FCSTD DOCUMENT  (FreeCAD 0.20R29410 (Git))
Label: ASM_Main
License: All rights reserved
LicenseURL: http://en.wikipedia.org/wiki/All_rights_reserved
objects: App::Link×4, App::DocumentObjectGroup×3, PartDesign::CoordinateSystem×1, App::FeaturePython×1, App::Part×1
note: 1 computed .brp shape members not serialized (recipe doc carries the construction recipe); baked Part::Feature solids carry a one-line shape summary decoded from their .brp
EXTERNAL_REF file=ASM_Base.FCStd obj=LCS_Origin
EXTERNAL_REF file=ASM_Base.FCStd obj=Assembly
EXTERNAL_REF file=ASM_Base.FCStd obj=PillowBlock_LCS_0
EXTERNAL_REF file=ASM_Platform.FCStd obj=ComputerPlatform_LCS_TopPivot
EXTERNAL_REF file=ASM_Platform.FCStd obj=Assembly
EXTERNAL_REF file=PlayStation5.FCStd obj=LCS_Origin
EXTERNAL_REF file=PlayStation5.FCStd obj=Assembly
EXTERNAL_REF file=ASM_DrivePlatform.FCStd obj=LCS_Origin
EXTERNAL_REF file=ASM_Platform.FCStd obj=LCS_Origin
EXTERNAL_REF file=ASM_DrivePlatform.FCStd obj=Assembly

FEATURE [App::DocumentObjectGroup] Parts
FEATURE [PartDesign::CoordinateSystem] LCS_Origin
  AttacherType = Attacher::AttachEngine3D
  MapMode = 2
  Support = -> [X_Axis]
FEATURE [App::FeaturePython] Variables  # WARN: FeaturePython — macro-defined, semantics opaque (R4)
  Type = App::PropertyContainer
FEATURE [App::DocumentObjectGroup] Constraints
FEATURE [App::DocumentObjectGroup] Configurations
FEATURE [App::Link] ASM_Base
  AttachedBy = #LCS_Origin
  AttachedTo = Parent Assembly#LCS_Origin
  LinkedObject = -> <external ASM_Base.FCStd>#Assembly
  SolverId = Asm4EE
  expr: Placement = LCS_Origin.Placement * AttachmentOffset * ASM_Base#LCS_Origin.Placement ^ -1
FEATURE [App::Link] ASM_Platform
  AttachedBy = #ComputerPlatform_LCS_TopPivot
  AttachedTo = ASM_Base#PillowBlock_LCS_0
  LinkPlacement = pos=(0,-1.75e-14,-124.8) rot=(0,0,1;0rad)
  LinkedObject = -> <external ASM_Platform.FCStd>#Assembly
  Placement = pos=(0,-1.75e-14,-124.8) rot=(0,0,1;0rad)
  SolverId = Asm4EE
  expr: Placement = ASM_Base.Placement * ASM_Base#PillowBlock_LCS_0.Placement * AttachmentOffset * ASM_Platform#ComputerPlatform_LCS_TopPivot.Placement ^ -1
FEATURE [App::Link] PlayStation5
  AttachedBy = #LCS_Origin
  AttachedTo = ASM_Platform#ComputerPlatform_LCS_TopPivot
  AttachmentOffset = pos=(0,-250,0) rot=(0,0,1;1.5708rad)
  LinkPlacement = pos=(0,-250,-106.3) rot=(0,0,-1;4.71239rad)
  LinkedObject = -> <external PlayStation5.FCStd>#Assembly
  Placement = pos=(0,-250,-106.3) rot=(0,0,-1;4.71239rad)
  SolverId = Asm4EE
  expr: Placement = ASM_Platform.Placement * ASM_Platform#ComputerPlatform_LCS_TopPivot.Placement * AttachmentOffset * PlayStation5#LCS_Origin.Placement ^ -1
FEATURE [App::Link] ASM_DrivePlatform
  AttachedBy = #LCS_Origin
  AttachedTo = ASM_Platform#LCS_Origin
  AttachmentOffset = pos=(0,0,69) rot=(0,0,1;0rad)
  LinkPlacement = pos=(0,-6e-16,-55.8) rot=(0,0,1;0rad)
  LinkedObject = -> <external ASM_DrivePlatform.FCStd>#Assembly
  Placement = pos=(0,-6e-16,-55.8) rot=(0,0,1;0rad)
  SolverId = Asm4EE
  expr: Placement = ASM_Platform.Placement * ASM_Platform#LCS_Origin.Placement * AttachmentOffset * ASM_DrivePlatform#LCS_Origin.Placement ^ -1
FEATURE [App::Part] Assembly
  AssemblyType = Part::Link
  Group = -> [LCS_Origin,Variables,Constraints,Configurations,ASM_Base,ASM_Platform,PlayStation5,ASM_DrivePlatform]
  Origin = -> Origin
  Type = Assembly

RESOLVED EXTERNAL PARTS (link-assembly join: the EXTERNAL_REF files above that resolve inside this repo's crawl, each included once):
---- part ASM_Base.FCStd = doc fcstd_288255adafcc ----
FCSTD DOCUMENT  (FreeCAD 0.20R29410 (Git))
Label: ASM_Base
License: All rights reserved
LicenseURL: http://en.wikipedia.org/wiki/All_rights_reserved
objects: App::Link×5, App::DocumentObjectGroup×3, PartDesign::CoordinateSystem×2, App::FeaturePython×1, App::Part×1
note: 2 computed .brp shape members not serialized (recipe doc carries the construction recipe); baked Part::Feature solids carry a one-line shape summary decoded from their .brp
EXTERNAL_REF file=MainWheel.FCStd obj=LCS_1
EXTERNAL_REF file=MainWheel.FCStd obj=Body
EXTERNAL_REF file=PipeFloorFlange.FCStd obj=LCS_1
EXTERNAL_REF file=PipeFloorFlange.FCStd obj=Body
EXTERNAL_REF file=PipeNipple.FCStd obj=LCS_root
EXTERNAL_REF file=PipeNipple.FCStd obj=Body
EXTERNAL_REF file=PillowBlock.FCStd obj=LCS_0
EXTERNAL_REF file=PipeNipple.FCStd obj=LCS_end
EXTERNAL_REF file=PillowBlock.FCStd obj=Body
EXTERNAL_REF file=SlipRing.FCStd obj=LCS_Origin
EXTERNAL_REF file=SlipRing.FCStd obj=Assembly

FEATURE [App::DocumentObjectGroup] Parts
FEATURE [PartDesign::CoordinateSystem] LCS_Origin
  AttacherType = Attacher::AttachEngine3D
  MapMode = 2
  Support = -> [X_Axis]
FEATURE [App::FeaturePython] Variables  # WARN: FeaturePython — macro-defined, semantics opaque (R4)
  Type = App::PropertyContainer
FEATURE [App::DocumentObjectGroup] Constraints
FEATURE [App::DocumentObjectGroup] Configurations
FEATURE [App::Link] MainWheel
  AssemblyType = Part::Link
  AttachedBy = #LCS_1
  AttachedTo = Parent Assembly#LCS_Origin
  LinkedObject = -> <external MainWheel.FCStd>#Body
  SolverId = Asm4EE
  expr: Placement = LCS_Origin.Placement * AttachmentOffset * MainWheel#LCS_1.Placement ^ -1
FEATURE [App::Link] PipeFlange
  AssemblyType = Part::Link
  AttachedBy = #LCS_1
  AttachedTo = MainWheel#LCS_1
  AttachmentOffset = pos=(0,0,0) rot=(1,0,0;3.14159rad)
  LinkPlacement = pos=(0,0,0) rot=(1,0,0;3.14159rad)
  LinkedObject = -> <external PipeFloorFlange.FCStd>#Body
  Placement = pos=(0,0,0) rot=(1,0,0;3.14159rad)
  SolverId = Asm4EE
  expr: Placement = MainWheel.Placement * MainWheel#LCS_1.Placement * AttachmentOffset * PipeFloorFlange#LCS_1.Placement ^ -1
FEATURE [App::Link] PipeNipple
  AssemblyType = Part::Link
  AttachedBy = #LCS_root
  AttachedTo = PipeFlange#LCS_1
  LinkPlacement = pos=(0,0,0) rot=(1,0,0;3.14159rad)
  LinkedObject = -> <external PipeNipple.FCStd>#Body
  Placement = pos=(0,0,0) rot=(1,0,0;3.14159rad)
  SolverId = Asm4EE
  expr: Placement = PipeFlange.Placement * PipeFloorFlange#LCS_1.Placement * AttachmentOffset * PipeNipple#LCS_root.Placement ^ -1
FEATURE [App::Link] PillowBlock
  AssemblyType = Part::Link
  AttachedBy = #LCS_0
  AttachedTo = PipeNipple#LCS_end
  AttachmentOffset = pos=(0,0,-8) rot=(1,0,0;3.14159rad)
  LinkPlacement = pos=(0,-1.3e-14,-106.3) rot=(0,0,1;0rad)
  LinkedObject = -> <external PillowBlock.FCStd>#Body
  Placement = pos=(0,-1.3e-14,-106.3) rot=(0,0,1;0rad)
  SolverId = Asm4EE
  expr: Placement = PipeNipple.Placement * PipeNipple#LCS_end.Placement * AttachmentOffset * PillowBlock#LCS_0.Placement ^ -1
FEATURE [PartDesign::CoordinateSystem] PillowBlock_LCS_0
  AttachedBy = Origin
  AttacherType = Attacher::AttachEngine3D
  Placement = pos=(0,-1.3e-14,-106.3) rot=(0,0,1;0rad)
  SolverId = Asm4EE
  expr: Placement = PillowBlock.Placement * PillowBlock#LCS_0.Placement
FEATURE [App::Link] SlipRing
  AttachedBy = #LCS_Origin
  AttachedTo = PipeNipple#LCS_end
  AttachmentOffset = pos=(0,0,0) rot=(1,0,0;3.14159rad)
  LinkPlacement = pos=(0,-1.4e-14,-114.3) rot=(0,0,1;0rad)
  LinkedObject = -> <external SlipRing.FCStd>#Assembly
  Placement = pos=(0,-1.4e-14,-114.3) rot=(0,0,1;0rad)
  SolverId = Asm4EE
  expr: Placement = PipeNipple.Placement * PipeNipple#LCS_end.Placement * AttachmentOffset * SlipRing#LCS_Origin.Placement ^ -1
FEATURE [App::Part] Assembly
  AssemblyType = Part::Link
  Group = -> [LCS_Origin,Variables,Constraints,Configurations,MainWheel,PipeFlange,PipeNipple,PillowBlock,PillowBlock_LCS_0,SlipRing]
  Origin = -> Origin
  Type = Assembly
---- part ASM_DrivePlatform.FCStd = doc fcstd_cc06b2823031 ----
FCSTD DOCUMENT  (FreeCAD 0.20R29410 (Git))
Label: ASM_DrivePlatform
License: All rights reserved
LicenseURL: http://en.wikipedia.org/wiki/All_rights_reserved
objects: App::DocumentObjectGroup×3, PartDesign::CoordinateSystem×3, App::Link×3, App::FeaturePython×1, App::Part×1
note: 3 computed .brp shape members not serialized (recipe doc carries the construction recipe); baked Part::Feature solids carry a one-line shape summary decoded from their .brp
EXTERNAL_REF file=Params.FCStd obj=Spreadsheet
EXTERNAL_REF file=ASM_DriveUnit.FCStd obj=LCS_Origin
EXTERNAL_REF file=ASM_DriveUnit.FCStd obj=Assembly
EXTERNAL_REF file=DrivePlatform.FCStd obj=LCS_Origin
EXTERNAL_REF file=DrivePlatform.FCStd obj=Assembly

FEATURE [App::DocumentObjectGroup] Parts
FEATURE [PartDesign::CoordinateSystem] LCS_Origin
  AttacherType = Attacher::AttachEngine3D
  MapMode = 2
  Support = -> [X_Axis]
FEATURE [App::FeaturePython] Variables  # WARN: FeaturePython — macro-defined, semantics opaque (R4)
  Type = App::PropertyContainer
FEATURE [App::DocumentObjectGroup] Constraints
FEATURE [App::DocumentObjectGroup] Configurations
FEATURE [PartDesign::CoordinateSystem] LCS_DriveUnit1
  AttacherType = Attacher::AttachEngine3D
  AttachmentOffset = pos=(0,0,0) rot=(0,0,1;0.523599rad)
  MapMode = 2
  Placement = pos=(0,0,0) rot=(0,0,1;0.523599rad)
  Support = -> [LCS_Origin]
  expr: .AttachmentOffset.Rotation.Angle = <<Params>>#<<Params>>.DriveUnitAngle
FEATURE [PartDesign::CoordinateSystem] LCS_DriveUnit002
  AttacherType = Attacher::AttachEngine3D
  AttachmentOffset = pos=(0,0,0) rot=(0,0,1;-0.523599rad)
  MapMode = 2
  Placement = pos=(0,0,0) rot=(0,0,1;5.75959rad)
  Support = -> [LCS_Origin]
  expr: .AttachmentOffset.Rotation.Angle = <<Params>>#<<Params>>.DriveUnitAngle * -1
FEATURE [App::Link] ASM_DriveUnit001
  AttachedBy = #LCS_Origin
  AttachedTo = Parent Assembly#LCS_DriveUnit1
  AttachmentOffset = pos=(0,280,0) rot=(0,0,1;0rad)
  LinkPlacement = pos=(-140,242.487,0) rot=(0,0,1;0.523599rad)
  LinkedObject = -> <external ASM_DriveUnit.FCStd>#Assembly
  Placement = pos=(-140,242.487,0) rot=(0,0,1;0.523599rad)
  SolverId = Asm4EE
  expr: .AttachmentOffset.Base.y = <<Params>>#<<Params>>.DriveRadius
  expr: Placement = LCS_DriveUnit1.Placement * AttachmentOffset * ASM_DriveUnit#LCS_Origin.Placement ^ -1
FEATURE [App::Link] ASM_DriveUnit002
  AttachedBy = #LCS_Origin
  AttachedTo = Parent Assembly#LCS_DriveUnit002
  AttachmentOffset = pos=(0,280,0) rot=(0,0,1;0rad)
  LinkPlacement = pos=(140,242.487,0) rot=(0,0,1;5.75959rad)
  LinkedObject = -> <external ASM_DriveUnit.FCStd>#Assembly
  Placement = pos=(140,242.487,0) rot=(0,0,1;5.75959rad)
  SolverId = Asm4EE
  expr: .AttachmentOffset.Base.y = <<Params>>#<<Params>>.DriveRadius
  expr: Placement = LCS_DriveUnit002.Placement * AttachmentOffset * ASM_DriveUnit#LCS_Origin.Placement ^ -1
FEATURE [App::Link] DrivePlatform
  AttachedBy = #LCS_Origin
  AttachedTo = Parent Assembly#LCS_Origin
  AttachmentOffset = pos=(0,0,0) rot=(0,1,0;3.14159rad)
  LinkPlacement = pos=(0,0,0) rot=(0,1,0;3.14159rad)
  LinkedObject = -> <external DrivePlatform.FCStd>#Assembly
  Placement = pos=(0,0,0) rot=(0,1,0;3.14159rad)
  SolverId = Asm4EE
  expr: Placement = LCS_Origin.Placement * AttachmentOffset * DrivePlatform#LCS_Origin.Placement ^ -1
FEATURE [App::Part] Assembly
  AssemblyType = Part::Link
  Group = -> [LCS_Origin,Variables,Constraints,Configurations,LCS_DriveUnit1,LCS_DriveUnit002,ASM_DriveUnit001,ASM_DriveUnit002,DrivePlatform]
  Origin = -> Origin
  Type = Assembly
---- part ASM_Platform.FCStd = doc fcstd_76b030723fdc ----
FCSTD DOCUMENT  (FreeCAD 0.20R29410 (Git))
Label: ASM_Platform
License: All rights reserved
LicenseURL: http://en.wikipedia.org/wiki/All_rights_reserved
objects: Part::FeaturePython×13, App::DocumentObjectGroup×4, App::Link×4, PartDesign::CoordinateSystem×2, App::FeaturePython×1, App::Part×1
note: 15 computed .brp shape members not serialized (recipe doc carries the construction recipe); baked Part::Feature solids carry a one-line shape summary decoded from their .brp
EXTERNAL_REF file=ComputerPlatform.FCStd obj=LCS_Origin
EXTERNAL_REF file=ComputerPlatform.FCStd obj=Assembly
EXTERNAL_REF file=ASM_GantrySkate.FCStd obj=LCS_Origin
EXTERNAL_REF file=Params.FCStd obj=Spreadsheet
EXTERNAL_REF file=ASM_GantrySkate.FCStd obj=Assembly
EXTERNAL_REF file=../../../../../AppData/Local/Temp/FreeCAD/Cache/FreeCAD_Doc_e326eb17-bc0b-4666-96ed-1d71e9908fb8_da39a3_8856 obj=LCS_Origin
EXTERNAL_REF file=../../../../../AppData/Local/Temp/FreeCAD/Cache/FreeCAD_Doc_e326eb17-bc0b-4666-96ed-1d71e9908fb8_da39a3_8856 obj=Assembly
EXTERNAL_REF file=AlExtrusion2040.FCStd obj=Assembly
EXTERNAL_REF file=ASM_ExtensionDriver.FCStd obj=LCS_Origin
EXTERNAL_REF file=ASM_ExtensionDriver.FCStd obj=Assembly
EXTERNAL_REF file=ComputerPlatform.FCStd obj=LCS_TopPivot
EXTERNAL_REF file=ComputerPlatform.FCStd obj=Pad
EXTERNAL_REF file=ComputerPlatform.FCStd obj=Body

FEATURE [App::DocumentObjectGroup] Parts
FEATURE [PartDesign::CoordinateSystem] LCS_Origin
  AttacherType = Attacher::AttachEngine3D
  MapMode = 2
  Support = -> [X_Axis]
FEATURE [App::FeaturePython] Variables  # WARN: FeaturePython — macro-defined, semantics opaque (R4)
  Type = App::PropertyContainer
FEATURE [App::DocumentObjectGroup] Constraints
FEATURE [App::DocumentObjectGroup] Configurations
FEATURE [App::Link] ComputerPlatform
  AttachedBy = #LCS_Origin
  AttachedTo = Parent Assembly#LCS_Origin
  LinkedObject = -> <external ComputerPlatform.FCStd>#Assembly
  SolverId = Asm4EE
  expr: Placement = LCS_Origin.Placement * AttachmentOffset * ComputerPlatform#LCS_Origin.Placement ^ -1
FEATURE [App::Link] ASM_GantrySkate  label="ASM_GantrySkate001"
  AttachedBy = #LCS_Origin
  AttachedTo = ComputerPlatform#LCS_Origin
  AttachmentOffset = pos=(20,-367,0) rot=(0,1,0;3.14159rad)
  LinkPlacement = pos=(20,-367,0) rot=(0,1,0;3.14159rad)
  LinkedObject = -> <external ASM_GantrySkate.FCStd>#Assembly
  Placement = pos=(20,-367,0) rot=(0,1,0;3.14159rad)
  SolverId = Asm4EE
  expr: .AttachmentOffset.Base.x = <<Params>>#<<Params>>.ExtensionArmCenterOffset
  expr: Placement = ComputerPlatform.Placement * ComputerPlatform#LCS_Origin.Placement * AttachmentOffset * ASM_GantrySkate#LCS_Origin.Placement ^ -1
FEATURE [App::Link] ASM_GantrySkate001  label="ASM_GantrySkate002"
  AttachedBy = #LCS_Origin
  AttachedTo = ComputerPlatform#LCS_Origin
  AttachmentOffset = pos=(20,192,0) rot=(0,1,0;3.14159rad)
  LinkPlacement = pos=(20,192,0) rot=(0,1,0;3.14159rad)
  LinkedObject = -> <external ASM_GantrySkate.FCStd>#Assembly
  Placement = pos=(20,192,0) rot=(0,1,0;3.14159rad)
  SolverId = Asm4EE
  expr: .AttachmentOffset.Base.x = <<Params>>#<<Params>>.ExtensionArmCenterOffset
  expr: Placement = ComputerPlatform.Placement * ComputerPlatform#LCS_Origin.Placement * AttachmentOffset * ASM_GantrySkate#LCS_Origin.Placement ^ -1
FEATURE [Part::FeaturePython] AlExtrusion2040_var  # link proxy (typed FeaturePython)
  AttachedBy = #LCS_Origin
  AttachedTo = ASM_GantrySkate#LCS_Origin
  AttachmentOffset = pos=(0,-30,23.5) rot=(0.57735,-0.57735,-0.57735;4.18879rad)
  Length = 2000
  LinkedObject = -> <external ../../../../../AppData/Local/Temp/FreeCAD/Cache/FreeCAD_Doc_e326eb17-bc0b-4666-96ed-1d71e9908fb8_da39a3_8856>#Assembly
  Placement = pos=(20,-397,-23.5) rot=(-0.57735,-0.57735,-0.57735;2.0944rad)
  SolverId = Asm4EE
  SourceObject = -> <external AlExtrusion2040.FCStd>#Assembly
  expr: Placement = ASM_GantrySkate.Placement * ASM_GantrySkate#LCS_Origin.Placement * AttachmentOffset * varTmpDoc_2#LCS_Origin.Placement ^ -1
FEATURE [App::Link] ASM_ExtensionDriver
  AttachedBy = #LCS_Origin
  AttachedTo = ComputerPlatform#LCS_Origin
  AttachmentOffset = pos=(-16,-300,0) rot=(0.707107,0.707107,0;3.14159rad)
  LinkPlacement = pos=(-16,-300,0) rot=(0.707107,0.707107,0;3.14159rad)
  LinkedObject = -> <external ASM_ExtensionDriver.FCStd>#Assembly
  Placement = pos=(-16,-300,0) rot=(0.707107,0.707107,0;3.14159rad)
  SolverId = Asm4EE
  expr: Placement = ComputerPlatform.Placement * ComputerPlatform#LCS_Origin.Placement * AttachmentOffset * ASM_ExtensionDriver#LCS_Origin.Placement ^ -1
FEATURE [PartDesign::CoordinateSystem] ComputerPlatform_LCS_TopPivot
  AttachedBy = Origin
  AttacherType = Attacher::AttachEngine3D
  Placement = pos=(0,0,18.5) rot=(0,0,1;0rad)
  SolverId = Asm4EE
  expr: Placement = ComputerPlatform.Placement * ComputerPlatform#LCS_TopPivot.Placement
FEATURE [Part::FeaturePython] Washer  label="M8-Washer"  # Fasteners workbench fastener (typed FeaturePython)
  Placement = pos=(163.744,212.613,0) rot=(-1,0,0;3.14159rad)
  diameter = 8
  invert = true
  matchOuter = false
  offset = 0
  type = 3
FEATURE [Part::FeaturePython] Washer001  label="M8-Washer005"  # Fasteners workbench fastener (typed FeaturePython)
  Placement = pos=(-163.744,212.613,0) rot=(-1,0,0;3.14159rad)
  diameter = 8
  invert = true
  matchOuter = false
  offset = 0
  type = 3
FEATURE [Part::FeaturePython] Washer002  label="M8-Washer004"  # Fasteners workbench fastener (typed FeaturePython)
  Placement = pos=(0,90,0) rot=(-1,0,0;3.14159rad)
  baseObject = -> <external ComputerPlatform.FCStd>#Pad [Edge53]
  diameter = 8
  invert = true
  matchOuter = false
  offset = 0
  type = 3
FEATURE [Part::FeaturePython] Screw  label="M8x75-Screw"  # Fasteners workbench fastener (typed FeaturePython)
  Placement = pos=(0,90,-1.8) rot=(-1,0,0;3.14159rad)
  baseObject = -> Washer002 [Edge1]
  diameter = 8
  invert = false
  length = 15
  lengthCustom = 75
  matchOuter = true
  offset = 0
  thread = false
  type = 34
FEATURE [Part::FeaturePython] Screw001  label="M8x75-Screw001"  # Fasteners workbench fastener (typed FeaturePython)
  Placement = pos=(-163.744,212.613,-1.8) rot=(-1,0,0;3.14159rad)
  baseObject = -> Washer001 [Edge1]
  diameter = 8
  invert = false
  length = 15
  lengthCustom = 75
  matchOuter = true
  offset = 0
  thread = false
  type = 34
FEATURE [Part::FeaturePython] Screw002  label="M8x75-Screw002"  # Fasteners workbench fastener (typed FeaturePython)
  Placement = pos=(163.744,212.613,-1.8) rot=(-1,0,0;3.14159rad)
  baseObject = -> Washer [Edge1]
  diameter = 8
  invert = false
  length = 15
  lengthCustom = 75
  matchOuter = true
  offset = 0
  thread = false
  type = 34
FEATURE [Part::FeaturePython] Washer003  label="M8-Washer006"  # Fasteners workbench fastener (typed FeaturePython)
  Placement = pos=(0,90,18.5) rot=(0,0,1;0rad)
  baseObject = -> <external ComputerPlatform.FCStd>#Body [Edge54]
  diameter = 8
  invert = false
  matchOuter = true
  offset = 0
  type = 3
FEATURE [Part::FeaturePython] Washer004  label="M8-Washer007"  # Fasteners workbench fastener (typed FeaturePython)
  Placement = pos=(163.744,212.613,18.5) rot=(0,0,1;0rad)
  baseObject = -> <external ComputerPlatform.FCStd>#Body [Edge60]
  diameter = 8
  invert = false
  matchOuter = true
  offset = 0
  type = 3
FEATURE [Part::FeaturePython] Washer005  label="M8-Washer008"  # Fasteners workbench fastener (typed FeaturePython)
  Placement = pos=(-163.744,212.613,18.5) rot=(0,0,1;0rad)
  baseObject = -> <external ComputerPlatform.FCStd>#Body [Edge57]
  diameter = 8
  invert = false
  matchOuter = true
  offset = 0
  type = 3
FEATURE [Part::FeaturePython] Nut  label="M8-Nut"  # Fasteners workbench fastener (typed FeaturePython)
  Placement = pos=(0,90,20.3) rot=(0,0,1;0rad)
  baseObject = -> Washer003 [Edge1]
  diameter = 6
  invert = false
  matchOuter = true
  offset = 0
  thread = false
  type = 5
FEATURE [Part::FeaturePython] Nut001  label="M8-Nut001"  # Fasteners workbench fastener (typed FeaturePython)
  Placement = pos=(163.744,212.613,20.3) rot=(0,0,1;0rad)
  baseObject = -> Washer004 [Edge1]
  diameter = 6
  invert = false
  matchOuter = true
  offset = 0
  thread = false
  type = 5
FEATURE [Part::FeaturePython] Nut002  label="M8-Nut002"  # Fasteners workbench fastener (typed FeaturePython)
  Placement = pos=(-163.744,212.613,20.3) rot=(0,0,1;0rad)
  baseObject = -> Washer005 [Edge1]
  diameter = 6
  invert = false
  matchOuter = true
  offset = 0
  thread = false
  type = 5
FEATURE [App::DocumentObjectGroup] Fasteners
  Group = -> [Washer,Washer001,Washer002,Screw,Screw001,Screw002,Washer003,Washer004,Washer005,Nut,Nut001,Nut002]
FEATURE [App::Part] Assembly
  AssemblyType = Part::Link
  Group = -> [LCS_Origin,Variables,Constraints,Configurations,ComputerPlatform,ASM_GantrySkate,ASM_GantrySkate001,AlExtrusion2040_var,ASM_ExtensionDriver,ComputerPlatform_LCS_TopPivot,Fasteners,Washer,Washer001,Washer002,Screw,Screw001,Screw002,Washer003,Washer004,Washer005,Nut,Nut001,Nut002]
  Origin = -> Origin
  Type = Assembly
---- part PlayStation5.FCStd = doc fcstd_1fe8443345a4 ----
FCSTD DOCUMENT  (FreeCAD 0.20R29410 (Git))
Label: PlayStation5
License: All rights reserved
LicenseURL: http://en.wikipedia.org/wiki/All_rights_reserved
objects: App::DocumentObjectGroup×3, PartDesign::CoordinateSystem×1, App::FeaturePython×1, Sketcher::SketchObject×1, PartDesign::Pad×1, PartDesign::Body×1, App::Part×1
note: 5 computed .brp shape members not serialized (recipe doc carries the construction recipe); baked Part::Feature solids carry a one-line shape summary decoded from their .brp

FEATURE [App::DocumentObjectGroup] Parts
FEATURE [PartDesign::CoordinateSystem] LCS_Origin
  AttacherType = Attacher::AttachEngine3D
  MapMode = 2
  Support = -> [X_Axis]
FEATURE [App::FeaturePython] Variables  # WARN: FeaturePython — macro-defined, semantics opaque (R4)
  Type = App::PropertyContainer
FEATURE [App::DocumentObjectGroup] Constraints
FEATURE [App::DocumentObjectGroup] Configurations
FEATURE [Sketcher::SketchObject] Sketch
  FullyConstrained = true
  MapMode = 5
  Support = -> [XY_Plane001]
  sketch-geometry (10):
    g0: ArcOfCircle CenterX=-121.54 CenterY=187.58 CenterZ=0 NormalX=0 NormalY=0 NormalZ=1 AngleXU=0 Radius=8 StartAngle=1.5708 EndAngle=3.14159
    g1: LineSegment StartX=-121.54 StartY=195.58 StartZ=0 EndX=121.54 EndY=195.58 EndZ=0
    g2: ArcOfCircle CenterX=121.54 CenterY=187.58 CenterZ=0 NormalX=0 NormalY=0 NormalZ=1 AngleXU=0 Radius=8 StartAngle=-9e-16 EndAngle=1.5708
    g3: LineSegment StartX=129.54 StartY=187.58 StartZ=0 EndX=129.54 EndY=-187.58 EndZ=0
    g4: ArcOfCircle CenterX=121.54 CenterY=-187.58 CenterZ=0 NormalX=0 NormalY=0 NormalZ=1 AngleXU=0 Radius=8 StartAngle=4.71239 EndAngle=6.28319
    g5: LineSegment StartX=121.54 StartY=-195.58 StartZ=0 EndX=-121.54 EndY=-195.58 EndZ=0
    g6: ArcOfCircle CenterX=-121.54 CenterY=-187.58 CenterZ=0 NormalX=0 NormalY=0 NormalZ=1 AngleXU=0 Radius=8 StartAngle=3.14159 EndAngle=4.71239
    g7: LineSegment StartX=-129.54 StartY=-187.58 StartZ=0 EndX=-129.54 EndY=187.58 EndZ=0
    g8: GeomPoint X=-129.54 Y=195.58 Z=0
    g9: GeomPoint X=129.54 Y=-195.58 Z=0
  constraints (23):
    c: Tangent(g0,g1) = 1.5708
    c: Tangent(g1,g2) = 1.5708
    c: Tangent(g2,g3) = 1.5708
    c: Tangent(g3,g4) = 1.5708
    c: Tangent(g4,g5) = 1.5708
    c: Tangent(g5,g6) = 1.5708
    c: Tangent(g6,g7) = 1.5708
    c: Tangent(g7,g0) = 1.5708
    c: Horizontal(g1)
    c: Horizontal(g5)
    c: Vertical(g3)
    c: Vertical(g7)
    c: Equal(g0,g2)
    c: Equal(g2,g4)
    c: Equal(g4,g6)
    c: PointOnObject(g8,g1)
    c: PointOnObject(g8,g7)
    c: PointOnObject(g9,g3)
    c: PointOnObject(g9,g5)
    c: Symmetric(g4,g0,g-1)
    c: Radius(g2) = 8
    c: DistanceX(g6,g3) = 259.08
    c: DistanceY(g4,g1) = 391.16
FEATURE [PartDesign::Pad] Pad
  Direction = (0,0,1)
  Length = 91.44
  Length2 = 10
  Profile = -> Sketch
  ReferenceAxis = -> Sketch [N_Axis]
  Type = 0
FEATURE [PartDesign::Body] Body
  Group = -> [Sketch,Pad]
  Origin = -> Origin001
  Tip = -> Pad
FEATURE [App::Part] Assembly
  AssemblyType = Part::Link
  Group = -> [LCS_Origin,Variables,Constraints,Configurations,Body]
  Origin = -> Origin
  Type = Assembly
